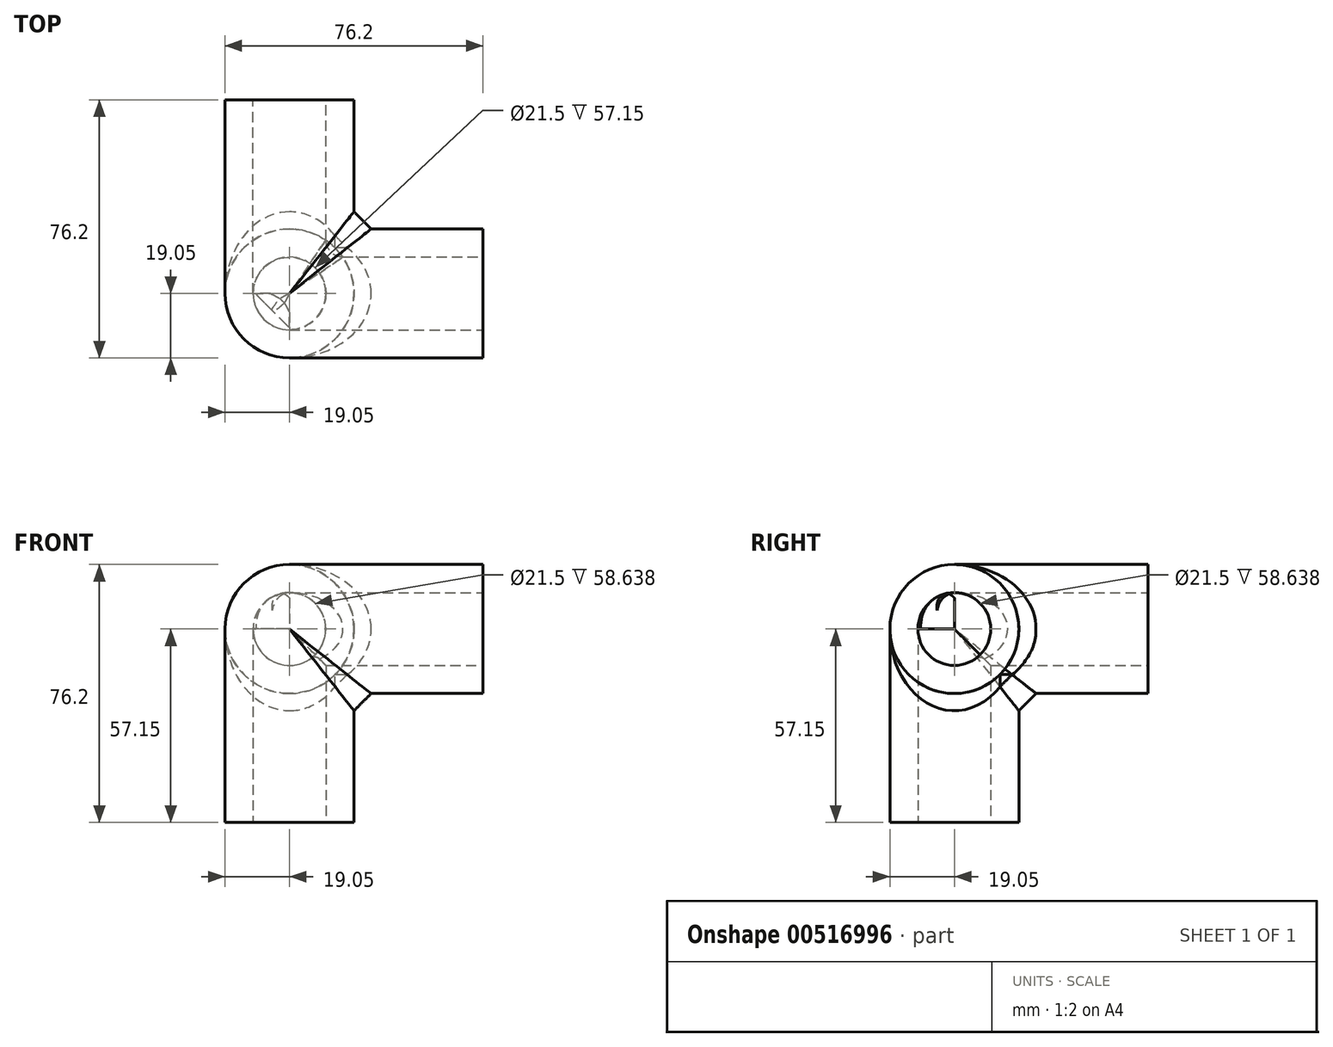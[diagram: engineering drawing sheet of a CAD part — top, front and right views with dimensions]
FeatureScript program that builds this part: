
annotation { "Feature Type Name" : "Feature", "Feature Type Description" : "" }
export const myFeature = defineFeature(function(context is Context, id is Id, definition is map)
    precondition{}
    {
        {
            var Q0;
            Q0=qCreatedBy(makeId("Front.planeOp"),FACE);
            var sketch = newSketch(context, id + "F0", { "sketchPlane" : qUnion([Q0])});
            skLineSegment(sketch, "E0.bottom", {"start": v(-19.05, 38.1) * mm, "end": v(19.05, 38.1) * mm});
            skLineSegment(sketch, "E0.top", {"start": v(-19.05, -38.1) * mm, "end": v(19.05, -38.1) * mm});
            skLineSegment(sketch, "E0.left", {"start": v(-19.05, 38.1) * mm, "end": v(-19.05, -38.1) * mm});
            skLineSegment(sketch, "E0.right", {"start": v(19.05, 38.1) * mm, "end": v(19.05, -38.1) * mm});
            skPoint(sketch, "E0.middle", {"position": v(0, 0) * mm});
            skLineSegment(sketch, "E1.bottom", {"start": v(19.05, 38.1) * mm, "end": v(57.15, 38.1) * mm});
            skLineSegment(sketch, "E1.top", {"start": v(19.05, 0) * mm, "end": v(57.15, 0) * mm});
            skLineSegment(sketch, "E1.left", {"start": v(19.05, 38.1) * mm, "end": v(19.05, 0) * mm});
            skLineSegment(sketch, "E1.right", {"start": v(57.15, 38.1) * mm, "end": v(57.15, 0) * mm});
            skSolve(sketch);
        }
        {
            var Q0;
            Q0 = qSketchRegion(id + "F0", true);
            extrude(context, id + "F1", {"entities" : qUnion([Q0]), "depth" : 38.1 * mm, "offsetDistance" : 25.4 * mm});
        }
        {
            var Q0;
            Q0=makeQuery(id+"F1.opExtrude","CAP_FACE",FACE,{"disambiguationData":[OSD([sQuery(id+"F0.wireOp",EDGE,"E0.bottom"),sQuery(id+"F0.wireOp",EDGE,"E0.top"),sQuery(id+"F0.wireOp",EDGE,"E0.left"),sQuery(id+"F0.wireOp",EDGE,"E0.right"),sQuery(id+"F0.wireOp",EDGE,"E1.bottom"),sQuery(id+"F0.wireOp",EDGE,"E1.top"),sQuery(id+"F0.wireOp",EDGE,"E1.right")])],"isStart":true});
            var sketch = newSketch(context, id + "F2", { "sketchPlane" : qUnion([Q0])});
            skLineSegment(sketch, "E2.bottom", {"start": v(19.05, 0) * mm, "end": v(-19.05, 0) * mm});
            skLineSegment(sketch, "E2.top", {"start": v(19.05, 38.1) * mm, "end": v(-19.05, 38.1) * mm});
            skLineSegment(sketch, "E2.left", {"start": v(19.05, 0) * mm, "end": v(19.05, 38.1) * mm});
            skLineSegment(sketch, "E2.right", {"start": v(-19.05, 0) * mm, "end": v(-19.05, 38.1) * mm});
            skSolve(sketch);
        }
        {
            var Q0;
            Q0=makeQuery(id+"F2.imprint","IMPRINT",FACE,{"disambiguationData":[TD([[makeQuery(id+"F2.imprint","IMPRINT",EDGE,{"derivedFrom":sQuery(id+"F2.wireOp",EDGE,"E2.bottom")}),-1.0]])]});
            extrude(context, id + "F3", {"entities" : qUnion([Q0]), "operationType" : NewBodyOperationType.ADD, "depth" : 38.1 * mm, "offsetDistance" : 25.4 * mm});
        }
        {
            var Q0;
            Q0=makeQuery(id+"F1.opExtrude","CAP_EDGE",EDGE,{"disambiguationData":[OSD([sQuery(id+"F0.wireOp",EDGE,"E0.bottom"),sQuery(id+"F0.wireOp",EDGE,"E1.bottom")])],"isStart":true});
            var Q1;
            Q1=makeQuery(id+"F1.opExtrude","CAP_EDGE",EDGE,{"disambiguationData":[OSD([sQuery(id+"F0.wireOp",EDGE,"E0.bottom"),sQuery(id+"F0.wireOp",EDGE,"E1.bottom")])],"isStart":false});
            var Q2;
            Q2=makeQuery(id+"F3.opExtrude","SWEPT_EDGE",EDGE,{"disambiguationData":[OSD([sQuery(id+"F0.wireOp",EDGE,"E0.bottom"),sQuery(id+"F0.wireOp",EDGE,"E1.bottom"),sQuery(id+"F2.wireOp",EDGE,"E2.top"),sQuery(id+"F2.wireOp",EDGE,"E2.right")])]});
            var Q3;
            Q3=makeQuery(id+"F1.opExtrude","CAP_EDGE",EDGE,{"disambiguationData":[OSD([sQuery(id+"F0.wireOp",EDGE,"E1.top")])],"isStart":true});
            var Q4;
            Q4=makeQuery(id+"F1.opExtrude","CAP_EDGE",EDGE,{"disambiguationData":[OSD([sQuery(id+"F0.wireOp",EDGE,"E1.top")])],"isStart":false});
            var Q5;
            Q5=makeQuery(id+"F3.boolean.opBoolean","MERGE",EDGE,{"derivedFrom":[makeQuery(id+"F1.opExtrude","SWEPT_EDGE",EDGE,{"disambiguationData":[OSD([sQuery(id+"F0.wireOp",EDGE,"E0.bottom"),sQuery(id+"F0.wireOp",EDGE,"E0.left")])]}),makeQuery(id+"F3.opExtrude","SWEPT_EDGE",EDGE,{"disambiguationData":[OSD([sQuery(id+"F2.wireOp",EDGE,"E2.top"),sQuery(id+"F2.wireOp",EDGE,"E2.left")])]})]});
            var Q6;
            Q6=makeQuery(id+"F3.opExtrude","SWEPT_EDGE",EDGE,{"disambiguationData":[OSD([sQuery(id+"F0.wireOp",EDGE,"E0.left"),sQuery(id+"F2.wireOp",EDGE,"E2.bottom"),sQuery(id+"F2.wireOp",EDGE,"E2.left")])]});
            var Q7;
            Q7=makeQuery(id+"F1.opExtrude","CAP_EDGE",EDGE,{"disambiguationData":[OSD([sQuery(id+"F0.wireOp",EDGE,"E0.left")])],"isStart":true});
            var Q8;
            Q8=makeQuery(id+"F1.opExtrude","CAP_EDGE",EDGE,{"disambiguationData":[OSD([sQuery(id+"F0.wireOp",EDGE,"E0.left")])],"isStart":false});
            fillet(context, id + "F4", {"entities" : qUnion([Q0, Q1, Q2, Q3, Q4, Q5, Q6, Q7, Q8]), "radius" : 19.05 * mm, "tangentPropagation" : true, "allowEdgeOverflow" : false});
        }
        {
            var Q0;
            Q0=makeQuery(id+"F1.opExtrude","CAP_EDGE",EDGE,{"disambiguationData":[OSD([sQuery(id+"F0.wireOp",EDGE,"E0.right")])],"isStart":false});
            var Q1;
            Q1=makeQuery(id+"F1.opExtrude","CAP_EDGE",EDGE,{"disambiguationData":[OSD([sQuery(id+"F0.wireOp",EDGE,"E0.right")])],"isStart":true});
            var Q2;
            Q2=makeQuery(id+"F3.opExtrude","SWEPT_EDGE",EDGE,{"disambiguationData":[OSD([sQuery(id+"F0.wireOp",EDGE,"E0.right"),sQuery(id+"F0.wireOp",EDGE,"E1.top"),sQuery(id+"F2.wireOp",EDGE,"E2.bottom"),sQuery(id+"F2.wireOp",EDGE,"E2.right")])]});
            fillet(context, id + "F5", {"entities" : qUnion([Q0, Q1, Q2]), "radius" : 19.05 * mm, "tangentPropagation" : true, "allowEdgeOverflow" : false});
        }
        {
            var Q0;
            Q0=makeQuery(id+"F3.opExtrude","CAP_FACE",FACE,{"disambiguationData":[OSD([sQuery(id+"F2.wireOp",EDGE,"E2.bottom"),sQuery(id+"F2.wireOp",EDGE,"E2.top"),sQuery(id+"F2.wireOp",EDGE,"E2.left"),sQuery(id+"F2.wireOp",EDGE,"E2.right")])],"isStart":false});
            var sketch = newSketch(context, id + "F6", { "sketchPlane" : qUnion([Q0])});
            skCircle(sketch, "E3", {"center": v(0, 19.05) * mm, "radius": 10.75 * mm});
            skSolve(sketch);
        }
        {
            var Q0;
            Q0=makeQuery(id+"F6.imprint","IMPRINT",FACE,{"disambiguationData":[TD([[makeQuery(id+"F6.imprint","IMPRINT",EDGE,{"derivedFrom":sQuery(id+"F6.wireOp",EDGE,"E3")}),1.0]])]});
            extrude(context, id + "F7", {"entities" : qUnion([Q0]), "operationType" : NewBodyOperationType.REMOVE, "oppositeDirection" : true, "depth" : 38.1 * mm, "offsetDistance" : 25.4 * mm});
        }
        {
            var Q0;
            Q0=makeQuery(id+"F1.opExtrude","SWEPT_FACE",FACE,{"disambiguationData":[OSD([sQuery(id+"F0.wireOp",EDGE,"E1.right")])]});
            var sketch = newSketch(context, id + "F8", { "sketchPlane" : qUnion([Q0])});
            skCircle(sketch, "E4", {"center": v(-19.05, 19.05) * mm, "radius": 10.75 * mm});
            skSolve(sketch);
        }
        {
            var Q0;
            Q0=makeQuery(id+"F8.imprint","IMPRINT",FACE,{"disambiguationData":[TD([[makeQuery(id+"F8.imprint","IMPRINT",EDGE,{"derivedFrom":sQuery(id+"F8.wireOp",EDGE,"E4")}),1.0]])]});
            extrude(context, id + "F9", {"entities" : qUnion([Q0]), "operationType" : NewBodyOperationType.REMOVE, "oppositeDirection" : true, "depth" : 38.1 * mm, "offsetDistance" : 25.4 * mm});
        }
        {
            var Q0;
            Q0=makeQuery(id+"F1.opExtrude","SWEPT_FACE",FACE,{"disambiguationData":[OSD([sQuery(id+"F0.wireOp",EDGE,"E0.top")])]});
            var sketch = newSketch(context, id + "F10", { "sketchPlane" : qUnion([Q0])});
            skCircle(sketch, "E5", {"center": v(0, 19.05) * mm, "radius": 10.75 * mm});
            skSolve(sketch);
        }
        {
            var Q0;
            Q0=makeQuery(id+"F10.imprint","IMPRINT",FACE,{"disambiguationData":[TD([[makeQuery(id+"F10.imprint","IMPRINT",EDGE,{"derivedFrom":sQuery(id+"F10.wireOp",EDGE,"E5")}),1.0]])]});
            extrude(context, id + "F11", {"entities" : qUnion([Q0]), "operationType" : NewBodyOperationType.REMOVE, "oppositeDirection" : true, "depth" : 38.1 * mm, "offsetDistance" : 25.4 * mm});
        }
        {
            var Q0;
            {var subQ0=sQuery(id+"F0.wireOp",EDGE,"E0.right");Q0=makeQuery(id+"F5.opFillet","BLEND_EDGE",EDGE,{"blendedFrom":[makeQuery(id+"F1.opExtrude","CAP_EDGE",EDGE,{"disambiguationData":[OSD([subQ0])],"isStart":true}),makeQuery(id+"F3.opExtrude","SWEPT_EDGE",EDGE,{"disambiguationData":[OSD([subQ0,sQuery(id+"F0.wireOp",EDGE,"E1.top"),sQuery(id+"F2.wireOp",EDGE,"E2.bottom"),sQuery(id+"F2.wireOp",EDGE,"E2.right")])]})],"blendedInto":[]});}
            var Q1;
            Q1=makeQuery(id+"F5.opFillet","BLEND_EDGE",EDGE,{"blendedFrom":[makeQuery(id+"F1.opExtrude","CAP_EDGE",EDGE,{"disambiguationData":[OSD([sQuery(id+"F0.wireOp",EDGE,"E0.right")])],"isStart":true}),makeQuery(id+"F4.opFillet","BLEND_FACE",FACE,{"disambiguationData":[OSD([sQuery(id+"F0.wireOp",EDGE,"E0.bottom"),sQuery(id+"F0.wireOp",EDGE,"E1.bottom")])]})],"blendedInto":[makeQuery(id+"F4.opFillet","BLEND_FACE",FACE,{"disambiguationData":[OSD([sQuery(id+"F0.wireOp",EDGE,"E0.bottom"),sQuery(id+"F0.wireOp",EDGE,"E1.bottom")])]})]});
            var Q2;
            Q2=makeQuery(id+"F5.opFillet","BLEND_EDGE",EDGE,{"blendedFrom":[makeQuery(id+"F3.opExtrude","SWEPT_EDGE",EDGE,{"disambiguationData":[OSD([sQuery(id+"F0.wireOp",EDGE,"E0.right"),sQuery(id+"F0.wireOp",EDGE,"E1.top"),sQuery(id+"F2.wireOp",EDGE,"E2.bottom"),sQuery(id+"F2.wireOp",EDGE,"E2.right")])]}),makeQuery(id+"F4.opFillet","BLEND_FACE",FACE,{"disambiguationData":[OSD([sQuery(id+"F0.wireOp",EDGE,"E0.bottom"),sQuery(id+"F0.wireOp",EDGE,"E1.bottom")])]})],"blendedInto":[makeQuery(id+"F4.opFillet","BLEND_FACE",FACE,{"disambiguationData":[OSD([sQuery(id+"F0.wireOp",EDGE,"E0.bottom"),sQuery(id+"F0.wireOp",EDGE,"E1.bottom")])]})]});
            chamfer(context, id + "F12", {"entities" : qUnion([Q0, Q1, Q2]), "width" : 5.08 * mm, "tangentPropagation" : true});
        }
        {
            var Q0;
            Q0=makeQuery(id+"F11.boolean.opBoolean","COPY",FACE,{"derivedFrom":makeQuery(id+"F11.opExtrude","CAP_FACE",FACE,{"disambiguationData":[OSD([sQuery(id+"F10.wireOp",EDGE,"E5")])],"isStart":false})});
            extrude(context, id + "F13", {"entities" : qUnion([Q0]), "operationType" : NewBodyOperationType.REMOVE, "oppositeDirection" : true, "depth" : 19.05 * mm, "offsetDistance" : 25.4 * mm});
        }
        {
            var Q0;
            Q0=makeQuery(id+"F7.boolean.opBoolean","COPY",FACE,{"derivedFrom":makeQuery(id+"F7.opExtrude","CAP_FACE",FACE,{"disambiguationData":[OSD([sQuery(id+"F6.wireOp",EDGE,"E3")])],"isStart":false})});
            extrude(context, id + "F14", {"entities" : qUnion([Q0]), "operationType" : NewBodyOperationType.REMOVE, "oppositeDirection" : true, "depth" : 19.05 * mm, "offsetDistance" : 25.4 * mm});
        }
        {
            var Q0;
            Q0=makeQuery(id+"F9.boolean.opBoolean","COPY",FACE,{"derivedFrom":makeQuery(id+"F9.opExtrude","CAP_FACE",FACE,{"disambiguationData":[OSD([sQuery(id+"F8.wireOp",EDGE,"E4")])],"isStart":false})});
            extrude(context, id + "F15", {"entities" : qUnion([Q0]), "operationType" : NewBodyOperationType.REMOVE, "oppositeDirection" : true, "depth" : 19.05 * mm, "offsetDistance" : 25.4 * mm});
        }
        {
            var Q0;
            Q0=makeQuery(id+"F15.boolean.opBoolean","INTERSECT",EDGE,{"derivedFrom":[makeQuery(id+"F14.boolean.opBoolean","COPY",FACE,{"derivedFrom":makeQuery(id+"F14.opExtrude","CAP_FACE",FACE,{"disambiguationData":[OSD([sQuery(id+"F6.wireOp",EDGE,"E3")])],"isStart":false})}),makeQuery(id+"F15.opExtrude","CAP_FACE",FACE,{"disambiguationData":[OSD([sQuery(id+"F8.wireOp",EDGE,"E4")])],"isStart":false})]});
            chamfer(context, id + "F16", {"entities" : qUnion([Q0]), "width" : 10.16 * mm, "tangentPropagation" : true});
        }
        {
            var Q0;
            {var subQ0=sQuery(id+"F6.wireOp",EDGE,"E3");Q0=makeQuery(id+"F15.boolean.opBoolean","INTERSECT",EDGE,{"derivedFrom":[makeQuery(id+"F14.boolean.opBoolean","MERGE",FACE,{"derivedFrom":[makeQuery(id+"FMOR63MR7ppFw8M_1.boolean.opBoolean","MERGE",FACE,{"derivedFrom":[makeQuery(id+"F7.boolean.opBoolean","COPY",FACE,{"derivedFrom":makeQuery(id+"F7.opExtrude","SWEPT_FACE",FACE,{"disambiguationData":[OSD([subQ0])]})}),makeQuery(id+"FMOR63MR7ppFw8M_1.opExtrude","SWEPT_FACE",FACE,{"disambiguationData":[OSD([subQ0])]})]}),makeQuery(id+"F14.opExtrude","SWEPT_FACE",FACE,{"disambiguationData":[OSD([subQ0])]})]}),makeQuery(id+"F15.opExtrude","SWEPT_FACE",FACE,{"disambiguationData":[OSD([sQuery(id+"F8.wireOp",EDGE,"E4")])]})]});}
            var Q1;
            {var subQ0=sQuery(id+"F6.wireOp",EDGE,"E3");Q1=makeQuery(id+"F16.opChamfer","BLEND_EDGE",EDGE,{"blendedFrom":[makeQuery(id+"F15.boolean.opBoolean","INTERSECT",EDGE,{"derivedFrom":[makeQuery(id+"F14.boolean.opBoolean","COPY",FACE,{"derivedFrom":makeQuery(id+"F14.opExtrude","CAP_FACE",FACE,{"disambiguationData":[OSD([subQ0])],"isStart":false})}),makeQuery(id+"F15.opExtrude","CAP_FACE",FACE,{"disambiguationData":[OSD([sQuery(id+"F8.wireOp",EDGE,"E4")])],"isStart":false})]}),makeQuery(id+"F14.boolean.opBoolean","MERGE",FACE,{"derivedFrom":[makeQuery(id+"FMOR63MR7ppFw8M_1.boolean.opBoolean","MERGE",FACE,{"derivedFrom":[makeQuery(id+"F7.boolean.opBoolean","COPY",FACE,{"derivedFrom":makeQuery(id+"F7.opExtrude","SWEPT_FACE",FACE,{"disambiguationData":[OSD([subQ0])]})}),makeQuery(id+"FMOR63MR7ppFw8M_1.opExtrude","SWEPT_FACE",FACE,{"disambiguationData":[OSD([subQ0])]})]}),makeQuery(id+"F14.opExtrude","SWEPT_FACE",FACE,{"disambiguationData":[OSD([subQ0])]})]})],"blendedInto":[makeQuery(id+"F14.boolean.opBoolean","MERGE",FACE,{"derivedFrom":[makeQuery(id+"FMOR63MR7ppFw8M_1.boolean.opBoolean","MERGE",FACE,{"derivedFrom":[makeQuery(id+"F7.boolean.opBoolean","COPY",FACE,{"derivedFrom":makeQuery(id+"F7.opExtrude","SWEPT_FACE",FACE,{"disambiguationData":[OSD([subQ0])]})}),makeQuery(id+"FMOR63MR7ppFw8M_1.opExtrude","SWEPT_FACE",FACE,{"disambiguationData":[OSD([subQ0])]})]}),makeQuery(id+"F14.opExtrude","SWEPT_FACE",FACE,{"disambiguationData":[OSD([subQ0])]})]})]});}
            var Q2;
            {var subQ0=sQuery(id+"F8.wireOp",EDGE,"E4");Q2=makeQuery(id+"F16.opChamfer","BLEND_EDGE",EDGE,{"blendedFrom":[makeQuery(id+"F15.boolean.opBoolean","INTERSECT",EDGE,{"derivedFrom":[makeQuery(id+"F14.boolean.opBoolean","COPY",FACE,{"derivedFrom":makeQuery(id+"F14.opExtrude","CAP_FACE",FACE,{"disambiguationData":[OSD([sQuery(id+"F6.wireOp",EDGE,"E3")])],"isStart":false})}),makeQuery(id+"F15.opExtrude","CAP_FACE",FACE,{"disambiguationData":[OSD([subQ0])],"isStart":false})]}),makeQuery(id+"F15.boolean.opBoolean","MERGE",FACE,{"derivedFrom":[makeQuery(id+"FjyXYSXNhCBdMaE_1.boolean.opBoolean","MERGE",FACE,{"derivedFrom":[makeQuery(id+"F9.boolean.opBoolean","COPY",FACE,{"derivedFrom":makeQuery(id+"F9.opExtrude","SWEPT_FACE",FACE,{"disambiguationData":[OSD([subQ0])]})}),makeQuery(id+"FjyXYSXNhCBdMaE_1.opExtrude","SWEPT_FACE",FACE,{"disambiguationData":[OSD([subQ0])]})]}),makeQuery(id+"F15.opExtrude","SWEPT_FACE",FACE,{"disambiguationData":[OSD([subQ0])]})]})],"blendedInto":[makeQuery(id+"F15.boolean.opBoolean","MERGE",FACE,{"derivedFrom":[makeQuery(id+"FjyXYSXNhCBdMaE_1.boolean.opBoolean","MERGE",FACE,{"derivedFrom":[makeQuery(id+"F9.boolean.opBoolean","COPY",FACE,{"derivedFrom":makeQuery(id+"F9.opExtrude","SWEPT_FACE",FACE,{"disambiguationData":[OSD([subQ0])]})}),makeQuery(id+"FjyXYSXNhCBdMaE_1.opExtrude","SWEPT_FACE",FACE,{"disambiguationData":[OSD([subQ0])]})]}),makeQuery(id+"F15.opExtrude","SWEPT_FACE",FACE,{"disambiguationData":[OSD([subQ0])]})]})]});}
            fillet(context, id + "F17", {"entities" : qUnion([Q0, Q1, Q2]), "radius" : 5.08 * mm, "tangentPropagation" : true, "allowEdgeOverflow" : false});
        }
    });
